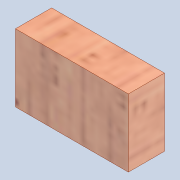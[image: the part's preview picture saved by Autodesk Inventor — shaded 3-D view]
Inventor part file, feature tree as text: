
AUTODESK INVENTOR PART (.ipt)
format: ipt  version: 2020 (Build 240168000, 168)  size: 101,888 bytes
history: native  units: mm
features: extrude x1, sketch x1
ambient origin geometry x8: Origin, YZ Plane, XZ Plane, XY Plane, X Axis, Y Axis, Z Axis, Center Point
bodies: Solid1 (feature_tree)
feature tree (2):
  extrude  "Extrusion1"  Depth=25.0mm
  sketch  "Sketch1"  dims[d0=15.0mm d1=25.0mm d2=8.0mm d3=0.0mm]
